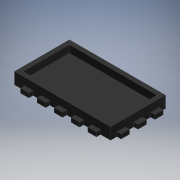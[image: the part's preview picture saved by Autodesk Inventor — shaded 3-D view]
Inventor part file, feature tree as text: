
AUTODESK INVENTOR PART (.ipt)
format: ipt  version: 2019 (Build 230136000, 136)  size: 250,880 bytes
history: native  units: mm
features: extrude x3, sketch x3, projected_geometry x1
ambient origin geometry x8: Origin, YZ Plane, XZ Plane, XY Plane, X Axis, Y Axis, Z Axis, Center Point
bodies: Solid1 (feature_tree)
feature tree (7):
  extrude  "Extrusion1"  Depth=60.0mm
  extrude  "Extrusion3"  Depth=4.0mm
  extrude  "Extrusion4"  Depth=4.0mm
  sketch  "Sketch1"  dims[d0=99.0mm d1=60.0mm]
  sketch  "Sketch3"  dims[d6=4.0mm d7=0.0mm d11=4.0mm]
  sketch  "Sketch5"  dims[d12=8.0mm d13=4.0mm d14=8.0mm d15=8.0mm d16=4.0mm d17=8.0mm d18=8.0mm d19=8.0mm d20=22.0mm d21=0.0mm d22=4.0mm d23=4.0mm d24=7.0mm d25=0.0mm]
  projected_geometry  "Projected Loop1"
